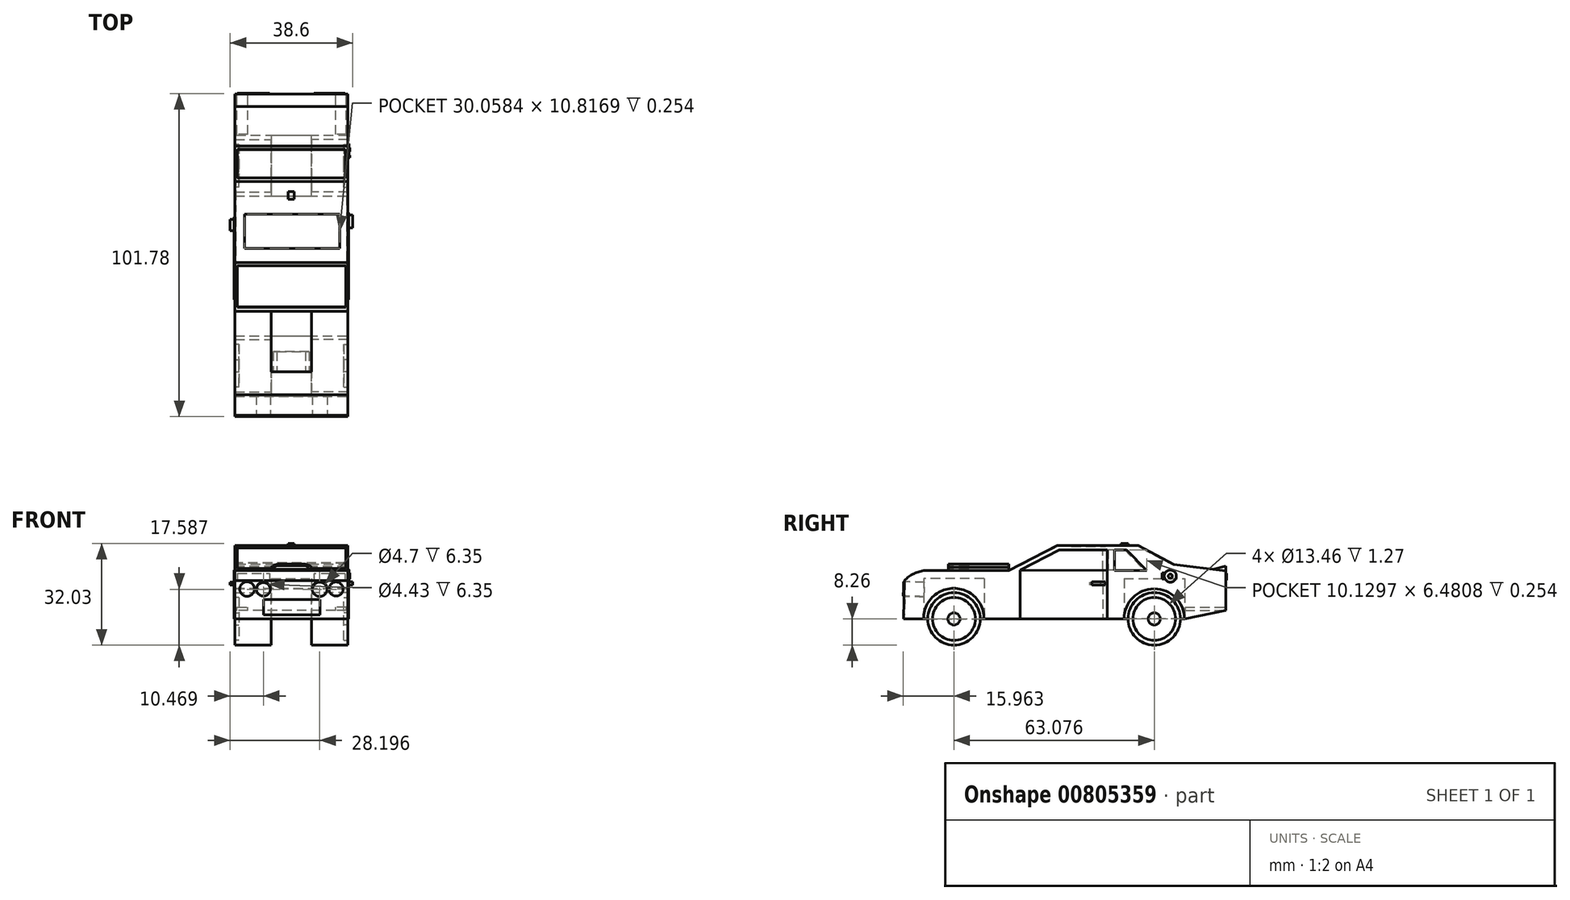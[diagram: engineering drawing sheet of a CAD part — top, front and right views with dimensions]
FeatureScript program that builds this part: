
annotation { "Feature Type Name" : "Feature", "Feature Type Description" : "" }
export const myFeature = defineFeature(function(context is Context, id is Id, definition is map)
    precondition{}
    {
        {
            var Q0;
            Q0=qCreatedBy(makeId("Right.planeOp"),FACE);
            var sketch = newSketch(context, id + "F0", { "sketchPlane" : qUnion([Q0])});
            skLineSegment(sketch, "E0", {"start": v(-101.04, 15.24) * mm, "end": v(-62.7, 15.24) * mm});
            skLineSegment(sketch, "E1", {"start": v(-62.7, 15.24) * mm, "end": v(-53, 23.14) * mm});
            skLineSegment(sketch, "E2", {"start": v(-53, 23.14) * mm, "end": v(-27.51, 23.14) * mm});
            skLineSegment(sketch, "E3", {"start": v(-27.51, 23.14) * mm, "end": v(-16.35, 17.16) * mm});
            skLineSegment(sketch, "E4", {"start": v(-16.35, 17.16) * mm, "end": v(0, 15.13) * mm});
            skLineSegment(sketch, "E5", {"start": v(0, 15.13) * mm, "end": v(0, 2.73) * mm});
            skLineSegment(sketch, "E6", {"start": v(0, 2.73) * mm, "end": v(-12.97, 0) * mm});
            skLineSegment(sketch, "E7", {"start": v(-12.97, 0) * mm, "end": v(-31.69, 0) * mm});
            skLineSegment(sketch, "E8", {"start": v(-31.69, 0) * mm, "end": v(-76.23, 0) * mm});
            skLineSegment(sketch, "E9", {"start": v(-76.23, 0) * mm, "end": v(-95.4, 0) * mm});
            skLineSegment(sketch, "E10", {"start": v(-95.4, 0) * mm, "end": v(-101.49, 0) * mm});
            skLineSegment(sketch, "E11", {"start": v(-101.49, 0) * mm, "end": v(-101.04, 15.24) * mm});
            skLineSegment(sketch, "E12", {"start": v(-53, 23.14) * mm, "end": v(-68.34, 15.24) * mm});
            skLineSegment(sketch, "E13", {"start": v(-68.34, 15.24) * mm, "end": v(-62.7, 15.24) * mm});
            skSolve(sketch);
        }
        {
            var Q0;
            Q0 = qSketchRegion(id + "F0", true);
            extrude(context, id + "F1", {"entities" : qUnion([Q0]), "depth" : 35.56 * mm, "offsetDistance" : 25.4 * mm});
        }
        {
            var Q0;
            Q0=makeQuery(id+"F1.opExtrude","CAP_FACE",FACE,{"disambiguationData":[OSD([sQuery(id+"F0.wireOp",EDGE,"E0"),sQuery(id+"F0.wireOp",EDGE,"E1"),sQuery(id+"F0.wireOp",EDGE,"E2"),sQuery(id+"F0.wireOp",EDGE,"E3"),sQuery(id+"F0.wireOp",EDGE,"E4"),sQuery(id+"F0.wireOp",EDGE,"E5"),sQuery(id+"F0.wireOp",EDGE,"E6"),sQuery(id+"F0.wireOp",EDGE,"E7"),sQuery(id+"F0.wireOp",EDGE,"E8"),sQuery(id+"F0.wireOp",EDGE,"E9"),sQuery(id+"F0.wireOp",EDGE,"E10"),sQuery(id+"F0.wireOp",EDGE,"E11")])],"isStart":false});
            var sketch = newSketch(context, id + "F2", { "sketchPlane" : qUnion([Q0])});
            skArc(sketch, "E14", {"start": v(-92.5, 15.24) * mm, "mid": v(-97.18, 14.66) * mm, "end": v(-101.13, 12.11) * mm});
            skSolve(sketch);
        }
        {
            var Q0;
            {var subQ0=sQuery(id+"F2.wireOp",EDGE,"E14");var subQ1=makeQuery(id+"F1.opExtrude","CAP_EDGE",EDGE,{"disambiguationData":[OSD([sQuery(id+"F0.wireOp",EDGE,"E11")])],"isStart":false});var subQ2=makeQuery(id+"F2.imprint","INTERSECT",VERTEX,{"derivedFrom":[subQ1,subQ0]});Q0=makeQuery(id+"F2.imprint","IMPRINT",FACE,{"disambiguationData":[TD([[makeQuery(id+"F2.imprint","IMPRINT",EDGE,{"disambiguationData":[TD([[subQ2,1.0]])],"derivedFrom":subQ0}),-1.0]])]});}
            extrude(context, id + "F3", {"entities" : qUnion([Q0]), "operationType" : NewBodyOperationType.REMOVE, "endBound" : BoundingType.THROUGH_ALL, "oppositeDirection" : true, "depth" : 25.4 * mm, "offsetDistance" : 25.4 * mm});
        }
        {
            var Q0;
            Q0=makeQuery(id+"F1.opExtrude","CAP_FACE",FACE,{"disambiguationData":[OSD([sQuery(id+"F0.wireOp",EDGE,"E0"),sQuery(id+"F0.wireOp",EDGE,"E1"),sQuery(id+"F0.wireOp",EDGE,"E2"),sQuery(id+"F0.wireOp",EDGE,"E3"),sQuery(id+"F0.wireOp",EDGE,"E4"),sQuery(id+"F0.wireOp",EDGE,"E5"),sQuery(id+"F0.wireOp",EDGE,"E6"),sQuery(id+"F0.wireOp",EDGE,"E7"),sQuery(id+"F0.wireOp",EDGE,"E8"),sQuery(id+"F0.wireOp",EDGE,"E9"),sQuery(id+"F0.wireOp",EDGE,"E10"),sQuery(id+"F0.wireOp",EDGE,"E11")])],"isStart":false});
            var sketch = newSketch(context, id + "F4", { "sketchPlane" : qUnion([Q0])});
            skLineSegment(sketch, "E15", {"start": v(-12.97, 0) * mm, "end": v(-32.02, 0) * mm, "construction": true});
            skLineSegment(sketch, "E16", {"start": v(-32.02, 0) * mm, "end": v(-22.5, 0) * mm, "construction": true});
            skLineSegment(sketch, "E17", {"start": v(-22.5, 0) * mm, "end": v(-22.5, 9.53) * mm, "construction": true});
            skLineSegment(sketch, "E18", {"start": v(-22.5, 9.53) * mm, "end": v(-22.5, -9.53) * mm, "construction": true});
            skLineSegment(sketch, "E19", {"start": v(-22.5, -9.53) * mm, "end": v(-22.5, 0) * mm, "construction": true});
            skLineSegment(sketch, "E20", {"start": v(-101.49, 0) * mm, "end": v(-95.14, 0) * mm, "construction": true});
            skLineSegment(sketch, "E21", {"start": v(-95.14, 0) * mm, "end": v(-76.09, 0) * mm, "construction": true});
            skLineSegment(sketch, "E22", {"start": v(-76.09, 0) * mm, "end": v(-85.61, 0) * mm, "construction": true});
            skLineSegment(sketch, "E23", {"start": v(-85.61, 0) * mm, "end": v(-85.61, 9.53) * mm, "construction": true});
            skLineSegment(sketch, "E24", {"start": v(-85.61, 9.53) * mm, "end": v(-85.61, -9.53) * mm, "construction": true});
            skArc(sketch, "E25", {"start": v(-76.09, 0) * mm, "mid": v(-85.61, 9.68) * mm, "end": v(-95.14, 0) * mm});
            skArc(sketch, "E26", {"start": v(-12.97, 0) * mm, "mid": v(-22.5, 9.51) * mm, "end": v(-32.02, 0) * mm});
            skLineSegment(sketch, "E27", {"start": v(-95.14, 0) * mm, "end": v(-76.09, 0) * mm});
            skLineSegment(sketch, "E28", {"start": v(-32.02, 0) * mm, "end": v(-12.97, 0) * mm});
            skArc(sketch, "E29", {"start": v(-76.09, 0) * mm, "mid": v(-85.61, 9.64) * mm, "end": v(-95.14, 0) * mm});
            skArc(sketch, "E30", {"start": v(-12.97, 0) * mm, "mid": v(-22.5, 9.49) * mm, "end": v(-32.02, 0) * mm});
            skSolve(sketch);
        }
        {
            var Q0;
            Q0=makeQuery(id+"F4.imprint","IMPRINT",FACE,{"disambiguationData":[TD([[makeQuery(id+"F4.imprint","IMPRINT",EDGE,{"derivedFrom":sQuery(id+"F4.wireOp",EDGE,"E27")}),-1.0]])]});
            var Q1;
            Q1=makeQuery(id+"F4.imprint","IMPRINT",FACE,{"disambiguationData":[TD([[makeQuery(id+"F4.imprint","IMPRINT",EDGE,{"derivedFrom":sQuery(id+"F4.wireOp",EDGE,"E28")}),-1.0]])]});
            extrude(context, id + "F5", {"entities" : qUnion([Q0, Q1]), "operationType" : NewBodyOperationType.REMOVE, "endBound" : BoundingType.THROUGH_ALL, "oppositeDirection" : true, "depth" : 25.4 * mm, "offsetDistance" : 25.4 * mm});
        }
        {
            var Q0;
            Q0=makeQuery(id+"F1.opExtrude","CAP_FACE",FACE,{"disambiguationData":[OSD([sQuery(id+"F0.wireOp",EDGE,"E0"),sQuery(id+"F0.wireOp",EDGE,"E1"),sQuery(id+"F0.wireOp",EDGE,"E2"),sQuery(id+"F0.wireOp",EDGE,"E3"),sQuery(id+"F0.wireOp",EDGE,"E4"),sQuery(id+"F0.wireOp",EDGE,"E5"),sQuery(id+"F0.wireOp",EDGE,"E6"),sQuery(id+"F0.wireOp",EDGE,"E7"),sQuery(id+"F0.wireOp",EDGE,"E8"),sQuery(id+"F0.wireOp",EDGE,"E9"),sQuery(id+"F0.wireOp",EDGE,"E10"),sQuery(id+"F0.wireOp",EDGE,"E11")])],"isStart":false});
            var sketch = newSketch(context, id + "F6", { "sketchPlane" : qUnion([Q0])});
            skLineSegment(sketch, "E31", {"start": v(0, 15.13) * mm, "end": v(0, 16.66) * mm});
            skLineSegment(sketch, "E32", {"start": v(0, 16.66) * mm, "end": v(-3.84, 15.6) * mm});
            skSolve(sketch);
        }
        {
            var Q0;
            {var subQ0=sQuery(id+"F6.wireOp",EDGE,"E31");Q0=makeQuery(id+"F6.imprint","IMPRINT",FACE,{"disambiguationData":[TD([[makeQuery(id+"F6.imprint","IMPRINT",EDGE,{"derivedFrom":subQ0}),1.0]])]});}
            extrude(context, id + "F7", {"entities" : qUnion([Q0]), "oppositeDirection" : true, "depth" : 35.56 * mm, "offsetDistance" : 25.4 * mm});
        }
        {
            var Q0;
            Q0=makeQuery(id+"F1.opExtrude","SWEPT_FACE",FACE,{"disambiguationData":[OSD([sQuery(id+"F0.wireOp",EDGE,"E2")])]});
            var sketch = newSketch(context, id + "F8", { "sketchPlane" : qUnion([Q0])});
            skLineSegment(sketch, "E33", {"start": v(17.78, -33.03) * mm, "end": v(18.6, -33.03) * mm});
            skPoint(sketch, "E33.startSnap0", {"position": v(17.78, -27.51) * mm});
            skLineSegment(sketch, "E34", {"start": v(18.6, -33.03) * mm, "end": v(18.6, -30.66) * mm});
            skLineSegment(sketch, "E35", {"start": v(18.6, -30.66) * mm, "end": v(16.76, -30.66) * mm});
            skLineSegment(sketch, "E36", {"start": v(16.76, -30.66) * mm, "end": v(16.76, -33.03) * mm});
            skLineSegment(sketch, "E37", {"start": v(16.76, -33.03) * mm, "end": v(17.78, -33.03) * mm});
            skSolve(sketch);
        }
        {
            var Q0;
            Q0 = qSketchRegion(id + "F8", true);
            extrude(context, id + "F9", {"entities" : qUnion([Q0]), "operationType" : NewBodyOperationType.ADD, "depth" : 0.64 * mm, "offsetDistance" : 25.4 * mm});
        }
        {
            var Q0;
            Q0=makeQuery(id+"F1.opExtrude","SWEPT_FACE",FACE,{"disambiguationData":[OSD([sQuery(id+"F0.wireOp",EDGE,"E2")])]});
            var sketch = newSketch(context, id + "F10", { "sketchPlane" : qUnion([Q0])});
            skLineSegment(sketch, "E38.bottom", {"start": v(2.98, -48.61) * mm, "end": v(33.04, -48.61) * mm});
            skLineSegment(sketch, "E38.top", {"start": v(2.98, -37.8) * mm, "end": v(33.04, -37.8) * mm});
            skLineSegment(sketch, "E38.left", {"start": v(2.98, -48.61) * mm, "end": v(2.98, -37.8) * mm});
            skLineSegment(sketch, "E38.right", {"start": v(33.04, -48.61) * mm, "end": v(33.04, -37.8) * mm});
            skSolve(sketch);
        }
        {
            var Q0;
            Q0 = qSketchRegion(id + "F10", true);
            extrude(context, id + "F11", {"entities" : qUnion([Q0]), "operationType" : NewBodyOperationType.REMOVE, "oppositeDirection" : true, "depth" : 0.25 * mm, "offsetDistance" : 25.4 * mm});
        }
        {
            var Q0;
            {var subQ2=sQuery(id+"F0.wireOp",EDGE,"E10");var subQ3=sQuery(id+"F0.wireOp",EDGE,"E9");var subQ4=sQuery(id+"F0.wireOp",EDGE,"E8");var subQ5=sQuery(id+"F0.wireOp",EDGE,"E7");Q0=makeQuery(id+"F5.boolean.opBoolean","SPLIT",FACE,{"disambiguationData":[TD([makeQuery(id+"F5.opExtrude","SWEPT_FACE",FACE,{"disambiguationData":[OSD([sQuery(id+"F4.wireOp",EDGE,"E30")])]})])],"derivedFrom":makeQuery(id+"F1.opExtrude","SWEPT_FACE",FACE,{"disambiguationData":[OSD([subQ5,subQ4,subQ3,subQ2])]})});}
            var sketch = newSketch(context, id + "F12", { "sketchPlane" : qUnion([Q0])});
            skLineSegment(sketch, "E39", {"start": v(17.78, 76.09) * mm, "end": v(24.13, 76.09) * mm});
            skLineSegment(sketch, "E40", {"start": v(24.13, 76.09) * mm, "end": v(11.43, 76.09) * mm});
            skLineSegment(sketch, "E41", {"start": v(11.43, 76.09) * mm, "end": v(11.43, 95.04) * mm});
            skLineSegment(sketch, "E42", {"start": v(11.43, 95.04) * mm, "end": v(24.13, 95.04) * mm});
            skLineSegment(sketch, "E43", {"start": v(24.13, 95.04) * mm, "end": v(24.13, 76.09) * mm});
            skSolve(sketch);
        }
        {
            var Q0;
            Q0 = qSketchRegion(id + "F12", true);
            extrude(context, id + "F13", {"entities" : qUnion([Q0]), "oppositeDirection" : true, "depth" : 12.7 * mm, "offsetDistance" : 25.4 * mm});
        }
        {
            var Q0;
            {var subQ2=sQuery(id+"F0.wireOp",EDGE,"E10");var subQ3=sQuery(id+"F0.wireOp",EDGE,"E9");var subQ4=sQuery(id+"F0.wireOp",EDGE,"E8");var subQ5=sQuery(id+"F0.wireOp",EDGE,"E7");Q0=makeQuery(id+"F5.boolean.opBoolean","SPLIT",FACE,{"disambiguationData":[TD([makeQuery(id+"F5.opExtrude","SWEPT_FACE",FACE,{"disambiguationData":[OSD([sQuery(id+"F4.wireOp",EDGE,"E30")])]})])],"derivedFrom":makeQuery(id+"F1.opExtrude","SWEPT_FACE",FACE,{"disambiguationData":[OSD([subQ5,subQ4,subQ3,subQ2])]})});}
            var sketch = newSketch(context, id + "F14", { "sketchPlane" : qUnion([Q0])});
            skLineSegment(sketch, "E44", {"start": v(17.78, 32.02) * mm, "end": v(11.43, 32.02) * mm});
            skLineSegment(sketch, "E45", {"start": v(11.43, 32.02) * mm, "end": v(24.13, 32.02) * mm});
            skLineSegment(sketch, "E46", {"start": v(24.13, 32.02) * mm, "end": v(24.13, 12.97) * mm});
            skLineSegment(sketch, "E47", {"start": v(24.13, 12.97) * mm, "end": v(11.43, 12.97) * mm});
            skLineSegment(sketch, "E48", {"start": v(11.43, 12.97) * mm, "end": v(11.43, 32.02) * mm});
            skSolve(sketch);
        }
        {
            var Q0;
            Q0 = qSketchRegion(id + "F14", true);
            extrude(context, id + "F15", {"entities" : qUnion([Q0]), "oppositeDirection" : true, "depth" : 12.7 * mm, "offsetDistance" : 25.4 * mm});
        }
        {
            var Q0;
            Q0=makeQuery(id+"F1.opExtrude","SWEPT_FACE",FACE,{"disambiguationData":[OSD([sQuery(id+"F0.wireOp",EDGE,"E12")])]});
            var sketch = newSketch(context, id + "F16", { "sketchPlane" : qUnion([Q0])});
            skLineSegment(sketch, "E49.bottom", {"start": v(0.7, -37.65) * mm, "end": v(34.9, -37.65) * mm});
            skLineSegment(sketch, "E49.top", {"start": v(0.7, -52.42) * mm, "end": v(34.9, -52.42) * mm});
            skLineSegment(sketch, "E49.left", {"start": v(0.7, -37.65) * mm, "end": v(0.7, -52.42) * mm});
            skLineSegment(sketch, "E49.right", {"start": v(34.9, -37.65) * mm, "end": v(34.9, -52.42) * mm});
            skSolve(sketch);
        }
        {
            var Q0;
            Q0 = qSketchRegion(id + "F16", true);
            extrude(context, id + "F17", {"entities" : qUnion([Q0]), "operationType" : NewBodyOperationType.REMOVE, "oppositeDirection" : true, "depth" : 0.25 * mm, "offsetDistance" : 25.4 * mm});
        }
        {
            var Q0;
            Q0=makeQuery(id+"F1.opExtrude","SWEPT_FACE",FACE,{"disambiguationData":[OSD([sQuery(id+"F0.wireOp",EDGE,"E0")])]});
            var sketch = newSketch(context, id + "F18", { "sketchPlane" : qUnion([Q0])});
            skLineSegment(sketch, "E50", {"start": v(17.78, -68.34) * mm, "end": v(24.13, -68.34) * mm});
            skLineSegment(sketch, "E51", {"start": v(24.13, -68.34) * mm, "end": v(11.43, -68.34) * mm});
            skLineSegment(sketch, "E52", {"start": v(11.43, -68.34) * mm, "end": v(11.43, -87.39) * mm});
            skLineSegment(sketch, "E53", {"start": v(11.43, -87.39) * mm, "end": v(24.13, -87.39) * mm});
            skLineSegment(sketch, "E54", {"start": v(24.13, -87.39) * mm, "end": v(24.13, -68.34) * mm});
            skSolve(sketch);
        }
        {
            var Q0;
            Q0 = qSketchRegion(id + "F18", true);
            extrude(context, id + "F19", {"entities" : qUnion([Q0]), "operationType" : NewBodyOperationType.ADD, "depth" : 2.03 * mm, "offsetDistance" : 25.4 * mm});
        }
        {
            var Q0;
            Q0=makeQuery(id+"F19.opExtrude","SWEPT_FACE",FACE,{"disambiguationData":[OSD([sQuery(id+"F18.wireOp",EDGE,"E53")])]});
            var sketch = newSketch(context, id + "F20", { "sketchPlane" : qUnion([Q0])});
            skLineSegment(sketch, "E55", {"start": v(11.43, 17.28) * mm, "end": v(13.97, 17.28) * mm, "construction": true});
            skLineSegment(sketch, "E56", {"start": v(24.13, 17.28) * mm, "end": v(21.6, 17.28) * mm, "construction": true});
            skArc(sketch, "E57", {"start": v(13.97, 17.28) * mm, "mid": v(12.6, 17.01) * mm, "end": v(11.43, 16.26) * mm});
            skArc(sketch, "E58", {"start": v(24.13, 16.26) * mm, "mid": v(22.96, 17.01) * mm, "end": v(21.6, 17.28) * mm});
            skLineSegment(sketch, "E59", {"start": v(11.43, 16.26) * mm, "end": v(11.43, 17.28) * mm});
            skLineSegment(sketch, "E60", {"start": v(24.13, 16.26) * mm, "end": v(24.13, 17.28) * mm});
            skSolve(sketch);
        }
        {
            var Q0;
            {var subQ0=sQuery(id+"F20.wireOp",EDGE,"E57");Q0=makeQuery(id+"F20.imprint","IMPRINT",FACE,{"disambiguationData":[TD([[makeQuery(id+"F20.imprint","IMPRINT",EDGE,{"derivedFrom":subQ0}),-1.0]])]});}
            var Q1;
            {var subQ0=sQuery(id+"F20.wireOp",EDGE,"E58");Q1=makeQuery(id+"F20.imprint","IMPRINT",FACE,{"disambiguationData":[TD([[makeQuery(id+"F20.imprint","IMPRINT",EDGE,{"derivedFrom":subQ0}),-1.0]])]});}
            extrude(context, id + "F21", {"entities" : qUnion([Q0, Q1]), "operationType" : NewBodyOperationType.REMOVE, "oppositeDirection" : true, "depth" : 19.05 * mm, "offsetDistance" : 25.4 * mm});
        }
        {
            var Q0;
            Q0=makeQuery(id+"F19.opExtrude","SWEPT_FACE",FACE,{"disambiguationData":[OSD([sQuery(id+"F18.wireOp",EDGE,"E53")])]});
            var sketch = newSketch(context, id + "F22", { "sketchPlane" : qUnion([Q0])});
            skLineSegment(sketch, "E61", {"start": v(12.1, 15.64) * mm, "end": v(12.1, 16.14) * mm});
            skLineSegment(sketch, "E62", {"start": v(12.1, 16.14) * mm, "end": v(13.23, 16.71) * mm});
            skLineSegment(sketch, "E63", {"start": v(13.23, 16.71) * mm, "end": v(22.2, 16.71) * mm});
            skLineSegment(sketch, "E64", {"start": v(22.2, 16.71) * mm, "end": v(23.34, 16.14) * mm});
            skLineSegment(sketch, "E65", {"start": v(23.34, 16.14) * mm, "end": v(23.34, 15.64) * mm});
            skLineSegment(sketch, "E66", {"start": v(23.34, 15.64) * mm, "end": v(12.1, 15.64) * mm});
            skSolve(sketch);
        }
        {
            var Q0;
            Q0 = qSketchRegion(id + "F22", true);
            extrude(context, id + "F23", {"entities" : qUnion([Q0]), "operationType" : NewBodyOperationType.REMOVE, "oppositeDirection" : true, "depth" : 6.35 * mm, "offsetDistance" : 25.4 * mm});
        }
        {
            var Q0;
            Q0=makeQuery(id+"F1.opExtrude","CAP_FACE",FACE,{"disambiguationData":[OSD([sQuery(id+"F0.wireOp",EDGE,"E0"),sQuery(id+"F0.wireOp",EDGE,"E2"),sQuery(id+"F0.wireOp",EDGE,"E3"),sQuery(id+"F0.wireOp",EDGE,"E4"),sQuery(id+"F0.wireOp",EDGE,"E5"),sQuery(id+"F0.wireOp",EDGE,"E6"),sQuery(id+"F0.wireOp",EDGE,"E7"),sQuery(id+"F0.wireOp",EDGE,"E8"),sQuery(id+"F0.wireOp",EDGE,"E9"),sQuery(id+"F0.wireOp",EDGE,"E10"),sQuery(id+"F0.wireOp",EDGE,"E11"),sQuery(id+"F0.wireOp",EDGE,"E12")])],"isStart":false});
            var sketch = newSketch(context, id + "F24", { "sketchPlane" : qUnion([Q0])});
            skCircle(sketch, "E67", {"center": v(-17.43, 13.49) * mm, "radius": 1.9 * mm});
            skSolve(sketch);
        }
        {
            var Q0;
            Q0 = qSketchRegion(id + "F24", true);
            extrude(context, id + "F25", {"entities" : qUnion([Q0]), "operationType" : NewBodyOperationType.ADD, "depth" : 0.38 * mm, "offsetDistance" : 25.4 * mm});
        }
        {
            var Q0;
            Q0=makeQuery(id+"F25.opExtrude","CAP_FACE",FACE,{"disambiguationData":[OSD([sQuery(id+"F24.wireOp",EDGE,"E67")])],"isStart":false});
            var sketch = newSketch(context, id + "F26", { "sketchPlane" : qUnion([Q0])});
            skCircle(sketch, "E68", {"center": v(-17.43, 13.49) * mm, "radius": 0.64 * mm});
            skSolve(sketch);
        }
        {
            var Q0;
            Q0 = qSketchRegion(id + "F26", true);
            extrude(context, id + "F27", {"entities" : qUnion([Q0]), "operationType" : NewBodyOperationType.ADD, "depth" : 0.25 * mm, "offsetDistance" : 25.4 * mm});
        }
        {
            var Q0;
            Q0=makeQuery(id+"F13.opExtrude","SWEPT_FACE",FACE,{"disambiguationData":[OSD([sQuery(id+"F12.wireOp",EDGE,"E43")])]});
            var sketch = newSketch(context, id + "F28", { "sketchPlane" : qUnion([Q0])});
            skCircle(sketch, "E69", {"center": v(-85.57, 0) * mm, "radius": 8.26 * mm});
            skSolve(sketch);
        }
        {
            var Q0;
            Q0 = qSketchRegion(id + "F28", true);
            extrude(context, id + "F29", {"entities" : qUnion([Q0]), "operationType" : NewBodyOperationType.ADD, "depth" : 11.43 * mm, "offsetDistance" : 25.4 * mm});
        }
        {
            var Q0;
            Q0=makeQuery(id+"F29.opExtrude","CAP_FACE",FACE,{"disambiguationData":[OSD([sQuery(id+"F28.wireOp",EDGE,"E69")])],"isStart":false});
            var sketch = newSketch(context, id + "F30", { "sketchPlane" : qUnion([Q0])});
            skCircle(sketch, "E70", {"center": v(-85.57, 0) * mm, "radius": 6.73 * mm});
            skSolve(sketch);
        }
        {
            var Q0;
            Q0 = qSketchRegion(id + "F30", true);
            extrude(context, id + "F31", {"entities" : qUnion([Q0]), "operationType" : NewBodyOperationType.REMOVE, "oppositeDirection" : true, "depth" : 1.27 * mm, "offsetDistance" : 25.4 * mm});
        }
        {
            var Q0;
            Q0=makeQuery(id+"F31.boolean.opBoolean","COPY",FACE,{"derivedFrom":makeQuery(id+"F31.opExtrude","CAP_FACE",FACE,{"disambiguationData":[OSD([sQuery(id+"F30.wireOp",EDGE,"E70")])],"isStart":false})});
            var sketch = newSketch(context, id + "F32", { "sketchPlane" : qUnion([Q0])});
            skCircle(sketch, "E71", {"center": v(-85.57, 0) * mm, "radius": 1.9 * mm});
            skSolve(sketch);
        }
        {
            var Q0;
            Q0 = qSketchRegion(id + "F32", true);
            extrude(context, id + "F33", {"entities" : qUnion([Q0]), "operationType" : NewBodyOperationType.ADD, "depth" : 1.27 * mm, "offsetDistance" : 25.4 * mm});
        }
        {
            var Q0;
            Q0=makeQuery(id+"F15.opExtrude","SWEPT_FACE",FACE,{"disambiguationData":[OSD([sQuery(id+"F14.wireOp",EDGE,"E46")])]});
            var sketch = newSketch(context, id + "F34", { "sketchPlane" : qUnion([Q0])});
            skCircle(sketch, "E72", {"center": v(-22.5, 0) * mm, "radius": 8.26 * mm});
            skSolve(sketch);
        }
        {
            var Q0;
            Q0 = qSketchRegion(id + "F34", true);
            extrude(context, id + "F35", {"entities" : qUnion([Q0]), "operationType" : NewBodyOperationType.ADD, "depth" : 11.43 * mm, "offsetDistance" : 25.4 * mm});
        }
        {
            var Q0;
            Q0=makeQuery(id+"F35.opExtrude","CAP_FACE",FACE,{"disambiguationData":[OSD([sQuery(id+"F34.wireOp",EDGE,"E72")])],"isStart":false});
            var sketch = newSketch(context, id + "F36", { "sketchPlane" : qUnion([Q0])});
            skCircle(sketch, "E73", {"center": v(-22.5, 0) * mm, "radius": 6.73 * mm});
            skSolve(sketch);
        }
        {
            var Q0;
            Q0 = qSketchRegion(id + "F36", true);
            extrude(context, id + "F37", {"entities" : qUnion([Q0]), "operationType" : NewBodyOperationType.REMOVE, "oppositeDirection" : true, "depth" : 1.27 * mm, "offsetDistance" : 25.4 * mm});
        }
        {
            var Q0;
            Q0=makeQuery(id+"F37.boolean.opBoolean","COPY",FACE,{"derivedFrom":makeQuery(id+"F37.opExtrude","CAP_FACE",FACE,{"disambiguationData":[OSD([sQuery(id+"F36.wireOp",EDGE,"E73")])],"isStart":false})});
            var sketch = newSketch(context, id + "F38", { "sketchPlane" : qUnion([Q0])});
            skCircle(sketch, "E74", {"center": v(-22.5, 0) * mm, "radius": 1.9 * mm});
            skSolve(sketch);
        }
        {
            var Q0;
            Q0 = qSketchRegion(id + "F38", true);
            extrude(context, id + "F39", {"entities" : qUnion([Q0]), "operationType" : NewBodyOperationType.ADD, "depth" : 1.27 * mm, "offsetDistance" : 25.4 * mm});
        }
        {
            var Q0;
            Q0=makeQuery(id+"F1.opExtrude","CAP_FACE",FACE,{"disambiguationData":[OSD([sQuery(id+"F0.wireOp",EDGE,"E0"),sQuery(id+"F0.wireOp",EDGE,"E2"),sQuery(id+"F0.wireOp",EDGE,"E3"),sQuery(id+"F0.wireOp",EDGE,"E4"),sQuery(id+"F0.wireOp",EDGE,"E5"),sQuery(id+"F0.wireOp",EDGE,"E6"),sQuery(id+"F0.wireOp",EDGE,"E7"),sQuery(id+"F0.wireOp",EDGE,"E8"),sQuery(id+"F0.wireOp",EDGE,"E9"),sQuery(id+"F0.wireOp",EDGE,"E10"),sQuery(id+"F0.wireOp",EDGE,"E11"),sQuery(id+"F0.wireOp",EDGE,"E12")])],"isStart":false});
            var sketch = newSketch(context, id + "F40", { "sketchPlane" : qUnion([Q0])});
            skArc(sketch, "E75", {"start": v(-19.19, 14.43) * mm, "mid": v(-19.4, 13.53) * mm, "end": v(-19.22, 12.61) * mm});
            skLineSegment(sketch, "E76", {"start": v(-19.22, 12.61) * mm, "end": v(-20.04, 12.61) * mm});
            skLineSegment(sketch, "E77", {"start": v(-20.04, 12.61) * mm, "end": v(-20.04, 14.42) * mm});
            skLineSegment(sketch, "E78", {"start": v(-20.04, 14.42) * mm, "end": v(-19.19, 14.43) * mm});
            skSolve(sketch);
        }
        {
            var Q0;
            Q0 = qSketchRegion(id + "F40", true);
            extrude(context, id + "F41", {"entities" : qUnion([Q0]), "operationType" : NewBodyOperationType.ADD, "depth" : 0.64 * mm, "offsetDistance" : 25.4 * mm});
        }
        {
            var Q0;
            Q0=makeQuery(id+"F15.opExtrude","SWEPT_FACE",FACE,{"disambiguationData":[OSD([sQuery(id+"F14.wireOp",EDGE,"E48")])]});
            var sketch = newSketch(context, id + "F42", { "sketchPlane" : qUnion([Q0])});
            skCircle(sketch, "E79", {"center": v(22.5, 0) * mm, "radius": 8.26 * mm});
            skSolve(sketch);
        }
        {
            var Q0;
            Q0 = qSketchRegion(id + "F42", true);
            extrude(context, id + "F43", {"entities" : qUnion([Q0]), "operationType" : NewBodyOperationType.ADD, "depth" : 11.43 * mm, "offsetDistance" : 25.4 * mm});
        }
        {
            var Q0;
            Q0=makeQuery(id+"F43.opExtrude","CAP_FACE",FACE,{"disambiguationData":[OSD([sQuery(id+"F42.wireOp",EDGE,"E79")])],"isStart":false});
            var sketch = newSketch(context, id + "F44", { "sketchPlane" : qUnion([Q0])});
            skCircle(sketch, "E80", {"center": v(22.5, 0) * mm, "radius": 6.73 * mm});
            skSolve(sketch);
        }
        {
            var Q0;
            Q0 = qSketchRegion(id + "F44", true);
            extrude(context, id + "F45", {"entities" : qUnion([Q0]), "operationType" : NewBodyOperationType.REMOVE, "oppositeDirection" : true, "depth" : 1.27 * mm, "offsetDistance" : 25.4 * mm});
        }
        {
            var Q0;
            Q0=makeQuery(id+"F45.boolean.opBoolean","COPY",FACE,{"derivedFrom":makeQuery(id+"F45.opExtrude","CAP_FACE",FACE,{"disambiguationData":[OSD([sQuery(id+"F44.wireOp",EDGE,"E80")])],"isStart":false})});
            var sketch = newSketch(context, id + "F46", { "sketchPlane" : qUnion([Q0])});
            skCircle(sketch, "E81", {"center": v(22.5, 0) * mm, "radius": 1.9 * mm});
            skSolve(sketch);
        }
        {
            var Q0;
            Q0 = qSketchRegion(id + "F46", true);
            extrude(context, id + "F47", {"entities" : qUnion([Q0]), "operationType" : NewBodyOperationType.ADD, "depth" : 1.27 * mm, "offsetDistance" : 25.4 * mm});
        }
        {
            var Q0;
            Q0=makeQuery(id+"F13.opExtrude","SWEPT_FACE",FACE,{"disambiguationData":[OSD([sQuery(id+"F12.wireOp",EDGE,"E41")])]});
            var sketch = newSketch(context, id + "F48", { "sketchPlane" : qUnion([Q0])});
            skCircle(sketch, "E82", {"center": v(85.57, 0) * mm, "radius": 8.26 * mm});
            skSolve(sketch);
        }
        {
            var Q0;
            {var subQ0=sQuery(id+"F48.wireOp",EDGE,"E82");var subQ1=makeQuery(id+"F13.opExtrude","CAP_EDGE",EDGE,{"disambiguationData":[OSD([sQuery(id+"F12.wireOp",EDGE,"E41")])],"isStart":true});var subQ2=makeQuery(id+"F48.imprint","INTERSECT",VERTEX,{"disambiguationData":[OD(0.0)],"derivedFrom":[subQ1,subQ0]});Q0=makeQuery(id+"F48.imprint","IMPRINT",FACE,{"disambiguationData":[TD([[makeQuery(id+"F48.imprint","IMPRINT",EDGE,{"disambiguationData":[TD([[subQ2,-1.0]])],"derivedFrom":subQ0}),1.0]])]});}
            var Q1;
            {var subQ0=sQuery(id+"F48.wireOp",EDGE,"E82");var subQ1=makeQuery(id+"F13.opExtrude","CAP_EDGE",EDGE,{"disambiguationData":[OSD([sQuery(id+"F12.wireOp",EDGE,"E41")])],"isStart":true});var subQ2=makeQuery(id+"F48.imprint","INTERSECT",VERTEX,{"disambiguationData":[OD(0.0)],"derivedFrom":[subQ1,subQ0]});Q1=makeQuery(id+"F48.imprint","IMPRINT",FACE,{"disambiguationData":[TD([[makeQuery(id+"F48.imprint","IMPRINT",EDGE,{"disambiguationData":[TD([[subQ2,1.0]])],"derivedFrom":subQ0}),1.0]])]});}
            extrude(context, id + "F49", {"entities" : qUnion([Q0, Q1]), "operationType" : NewBodyOperationType.ADD, "depth" : 11.43 * mm, "offsetDistance" : 25.4 * mm});
        }
        {
            var Q0;
            Q0=makeQuery(id+"F49.opExtrude","CAP_FACE",FACE,{"disambiguationData":[OSD([sQuery(id+"F48.wireOp",EDGE,"E82")])],"isStart":false});
            var sketch = newSketch(context, id + "F50", { "sketchPlane" : qUnion([Q0])});
            skCircle(sketch, "E83", {"center": v(85.57, 0) * mm, "radius": 6.73 * mm});
            skSolve(sketch);
        }
        {
            var Q0;
            Q0=makeQuery(id+"F50.imprint","IMPRINT",FACE,{"disambiguationData":[TD([[makeQuery(id+"F50.imprint","IMPRINT",EDGE,{"derivedFrom":sQuery(id+"F50.wireOp",EDGE,"E83")}),1.0]])]});
            extrude(context, id + "F51", {"entities" : qUnion([Q0]), "operationType" : NewBodyOperationType.REMOVE, "oppositeDirection" : true, "depth" : 1.27 * mm, "offsetDistance" : 25.4 * mm});
        }
        {
            var Q0;
            Q0=makeQuery(id+"F51.boolean.opBoolean","COPY",FACE,{"derivedFrom":makeQuery(id+"F51.opExtrude","CAP_FACE",FACE,{"disambiguationData":[OSD([sQuery(id+"F50.wireOp",EDGE,"E83")])],"isStart":false})});
            var sketch = newSketch(context, id + "F52", { "sketchPlane" : qUnion([Q0])});
            skCircle(sketch, "E84", {"center": v(85.57, 0) * mm, "radius": 1.9 * mm});
            skSolve(sketch);
        }
        {
            var Q0;
            Q0 = qSketchRegion(id + "F52", true);
            extrude(context, id + "F53", {"entities" : qUnion([Q0]), "operationType" : NewBodyOperationType.ADD, "depth" : 1.27 * mm, "offsetDistance" : 25.4 * mm});
        }
        {
            var Q0;
            Q0=makeQuery(id+"F1.opExtrude","CAP_FACE",FACE,{"disambiguationData":[OSD([sQuery(id+"F0.wireOp",EDGE,"E0"),sQuery(id+"F0.wireOp",EDGE,"E2"),sQuery(id+"F0.wireOp",EDGE,"E3"),sQuery(id+"F0.wireOp",EDGE,"E4"),sQuery(id+"F0.wireOp",EDGE,"E5"),sQuery(id+"F0.wireOp",EDGE,"E6"),sQuery(id+"F0.wireOp",EDGE,"E7"),sQuery(id+"F0.wireOp",EDGE,"E8"),sQuery(id+"F0.wireOp",EDGE,"E9"),sQuery(id+"F0.wireOp",EDGE,"E10"),sQuery(id+"F0.wireOp",EDGE,"E11"),sQuery(id+"F0.wireOp",EDGE,"E12")])],"isStart":false});
            var sketch = newSketch(context, id + "F54", { "sketchPlane" : qUnion([Q0])});
            skLineSegment(sketch, "E85", {"start": v(-64.77, 15.36) * mm, "end": v(-52.4, 21.73) * mm});
            skLineSegment(sketch, "E86", {"start": v(-52.4, 21.73) * mm, "end": v(-31.2, 21.73) * mm});
            skLineSegment(sketch, "E87", {"start": v(-31.2, 21.73) * mm, "end": v(-24.9, 15.24) * mm});
            skLineSegment(sketch, "E88", {"start": v(-24.9, 15.24) * mm, "end": v(-65.9, 15.36) * mm});
            skLineSegment(sketch, "E89", {"start": v(-34.58, 21.73) * mm, "end": v(-34.58, 15.27) * mm});
            skLineSegment(sketch, "E90", {"start": v(-34.58, 15.27) * mm, "end": v(-34.58, 0) * mm});
            skLineSegment(sketch, "E91", {"start": v(-34.58, 0) * mm, "end": v(-64.77, 0) * mm});
            skLineSegment(sketch, "E92", {"start": v(-64.77, 0) * mm, "end": v(-64.77, 15.36) * mm});
            skSolve(sketch);
        }
        {
            var Q0;
            {var subQ2=sQuery(id+"F54.wireOp",EDGE,"E85");Q0=makeQuery(id+"F54.imprint","IMPRINT",FACE,{"disambiguationData":[TD([[makeQuery(id+"F54.imprint","IMPRINT",EDGE,{"derivedFrom":subQ2}),-1.0]])]});}
            var Q1;
            {var subQ0=sQuery(id+"F54.wireOp",EDGE,"E87");Q1=makeQuery(id+"F54.imprint","IMPRINT",FACE,{"disambiguationData":[TD([[makeQuery(id+"F54.imprint","IMPRINT",EDGE,{"derivedFrom":subQ0}),-1.0]])]});}
            extrude(context, id + "F55", {"entities" : qUnion([Q0, Q1]), "operationType" : NewBodyOperationType.REMOVE, "oppositeDirection" : true, "depth" : 0.25 * mm, "offsetDistance" : 25.4 * mm});
        }
        {
            var Q0;
            Q0=makeQuery(id+"F55.boolean.opBoolean","COPY",FACE,{"derivedFrom":makeQuery(id+"F55.opExtrude","CAP_FACE",FACE,{"disambiguationData":[OSD([sQuery(id+"F54.wireOp",EDGE,"E85"),sQuery(id+"F54.wireOp",EDGE,"E86"),sQuery(id+"F54.wireOp",EDGE,"E87"),sQuery(id+"F54.wireOp",EDGE,"E88"),sQuery(id+"F54.wireOp",EDGE,"E92")])],"isStart":false})});
            var sketch = newSketch(context, id + "F56", { "sketchPlane" : qUnion([Q0])});
            skLineSegment(sketch, "E93", {"start": v(-35.02, 21.73) * mm, "end": v(-35.02, 15.27) * mm});
            skLineSegment(sketch, "E94", {"start": v(-35.02, 15.27) * mm, "end": v(-37.24, 15.28) * mm});
            skLineSegment(sketch, "E95", {"start": v(-37.24, 15.28) * mm, "end": v(-37.24, 21.73) * mm});
            skLineSegment(sketch, "E96", {"start": v(-37.24, 21.73) * mm, "end": v(-35.02, 21.73) * mm});
            skSolve(sketch);
        }
        {
            var Q0;
            Q0=makeQuery(id+"F56.imprint","IMPRINT",FACE,{"disambiguationData":[TD([[makeQuery(id+"F56.imprint","IMPRINT",EDGE,{"derivedFrom":sQuery(id+"F56.wireOp",EDGE,"E93")}),-1.0]])]});
            extrude(context, id + "F57", {"entities" : qUnion([Q0]), "operationType" : NewBodyOperationType.ADD, "depth" : 0.25 * mm, "offsetDistance" : 25.4 * mm});
        }
        {
            var Q0;
            Q0=makeQuery(id+"F57.boolean.opBoolean","MERGE",FACE,{"derivedFrom":[makeQuery(id+"F1.opExtrude","CAP_FACE",FACE,{"disambiguationData":[OSD([sQuery(id+"F0.wireOp",EDGE,"E0"),sQuery(id+"F0.wireOp",EDGE,"E2"),sQuery(id+"F0.wireOp",EDGE,"E3"),sQuery(id+"F0.wireOp",EDGE,"E4"),sQuery(id+"F0.wireOp",EDGE,"E5"),sQuery(id+"F0.wireOp",EDGE,"E6"),sQuery(id+"F0.wireOp",EDGE,"E7"),sQuery(id+"F0.wireOp",EDGE,"E8"),sQuery(id+"F0.wireOp",EDGE,"E9"),sQuery(id+"F0.wireOp",EDGE,"E10"),sQuery(id+"F0.wireOp",EDGE,"E11"),sQuery(id+"F0.wireOp",EDGE,"E12")])],"isStart":false}),makeQuery(id+"F57.opExtrude","CAP_FACE",FACE,{"disambiguationData":[OSD([sQuery(id+"F56.wireOp",EDGE,"E93"),sQuery(id+"F56.wireOp",EDGE,"E94"),sQuery(id+"F56.wireOp",EDGE,"E95"),sQuery(id+"F56.wireOp",EDGE,"E96")])],"isStart":false})]});
            var sketch = newSketch(context, id + "F58", { "sketchPlane" : qUnion([Q0])});
            skLineSegment(sketch, "E97", {"start": v(-37.24, 15.28) * mm, "end": v(-37.24, 0) * mm});
            skLineSegment(sketch, "E98", {"start": v(-37.24, 0) * mm, "end": v(-64.77, 0) * mm});
            skLineSegment(sketch, "E99", {"start": v(-64.77, 0) * mm, "end": v(-64.77, 15.36) * mm});
            skSolve(sketch);
        }
        {
            var Q0;
            Q0=makeQuery(id+"F58.imprint","IMPRINT",FACE,{"disambiguationData":[TD([[makeQuery(id+"F58.imprint","IMPRINT",EDGE,{"derivedFrom":sQuery(id+"F58.wireOp",EDGE,"E97")}),-1.0]])]});
            extrude(context, id + "F59", {"entities" : qUnion([Q0]), "operationType" : NewBodyOperationType.ADD, "depth" : 0.25 * mm, "offsetDistance" : 25.4 * mm});
        }
        {
            var Q0;
            Q0=makeQuery(id+"F59.opExtrude","CAP_FACE",FACE,{"disambiguationData":[OSD([sQuery(id+"F54.wireOp",EDGE,"E88"),sQuery(id+"F58.wireOp",EDGE,"E97"),sQuery(id+"F58.wireOp",EDGE,"E98"),sQuery(id+"F58.wireOp",EDGE,"E99")])],"isStart":false});
            var sketch = newSketch(context, id + "F60", { "sketchPlane" : qUnion([Q0])});
            skLineSegment(sketch, "E100.bottom", {"start": v(-42.1, 11.64) * mm, "end": v(-38, 11.64) * mm});
            skLineSegment(sketch, "E100.top", {"start": v(-42.1, 10.73) * mm, "end": v(-38, 10.73) * mm});
            skLineSegment(sketch, "E100.left", {"start": v(-42.1, 11.64) * mm, "end": v(-42.1, 10.73) * mm});
            skLineSegment(sketch, "E100.right", {"start": v(-38, 11.64) * mm, "end": v(-38, 10.73) * mm});
            skSolve(sketch);
        }
        {
            var Q0;
            Q0=makeQuery(id+"F60.imprint","IMPRINT",FACE,{"disambiguationData":[TD([[makeQuery(id+"F60.imprint","IMPRINT",EDGE,{"derivedFrom":sQuery(id+"F60.wireOp",EDGE,"E100.bottom")}),-1.0]])]});
            extrude(context, id + "F61", {"entities" : qUnion([Q0]), "operationType" : NewBodyOperationType.ADD, "depth" : 1.27 * mm, "offsetDistance" : 25.4 * mm});
        }
        {
            var Q0;
            Q0=makeQuery(id+"F1.opExtrude","SWEPT_FACE",FACE,{"disambiguationData":[OSD([sQuery(id+"F0.wireOp",EDGE,"E3")])]});
            var sketch = newSketch(context, id + "F62", { "sketchPlane" : qUnion([Q0])});
            skLineSegment(sketch, "E101.bottom", {"start": v(34.74, -33.87) * mm, "end": v(0.72, -33.87) * mm});
            skLineSegment(sketch, "E101.top", {"start": v(34.74, -23.65) * mm, "end": v(0.72, -23.65) * mm});
            skLineSegment(sketch, "E101.left", {"start": v(34.74, -33.87) * mm, "end": v(34.74, -23.65) * mm});
            skLineSegment(sketch, "E101.right", {"start": v(0.72, -33.87) * mm, "end": v(0.72, -23.65) * mm});
            skSolve(sketch);
        }
        {
            var Q0;
            Q0=makeQuery(id+"F62.imprint","IMPRINT",FACE,{"disambiguationData":[TD([[makeQuery(id+"F62.imprint","IMPRINT",EDGE,{"derivedFrom":sQuery(id+"F62.wireOp",EDGE,"E101.bottom")}),-1.0]])]});
            extrude(context, id + "F63", {"entities" : qUnion([Q0]), "operationType" : NewBodyOperationType.REMOVE, "oppositeDirection" : true, "depth" : 0.25 * mm, "offsetDistance" : 25.4 * mm});
        }
        {
            var Q0;
            Q0=makeQuery(id+"F1.opExtrude","CAP_FACE",FACE,{"disambiguationData":[OSD([sQuery(id+"F0.wireOp",EDGE,"E0"),sQuery(id+"F0.wireOp",EDGE,"E2"),sQuery(id+"F0.wireOp",EDGE,"E3"),sQuery(id+"F0.wireOp",EDGE,"E4"),sQuery(id+"F0.wireOp",EDGE,"E5"),sQuery(id+"F0.wireOp",EDGE,"E6"),sQuery(id+"F0.wireOp",EDGE,"E7"),sQuery(id+"F0.wireOp",EDGE,"E8"),sQuery(id+"F0.wireOp",EDGE,"E9"),sQuery(id+"F0.wireOp",EDGE,"E10"),sQuery(id+"F0.wireOp",EDGE,"E11"),sQuery(id+"F0.wireOp",EDGE,"E12")])],"isStart":true});
            var sketch = newSketch(context, id + "F64", { "sketchPlane" : qUnion([Q0])});
            skLineSegment(sketch, "E102", {"start": v(64.4, 15.2) * mm, "end": v(52.62, 21.88) * mm});
            skLineSegment(sketch, "E103", {"start": v(52.62, 21.88) * mm, "end": v(31.87, 21.88) * mm});
            skLineSegment(sketch, "E104", {"start": v(31.87, 21.88) * mm, "end": v(25.75, 15.4) * mm});
            skLineSegment(sketch, "E105", {"start": v(25.75, 15.4) * mm, "end": v(64.4, 15.2) * mm});
            skSolve(sketch);
        }
        {
            var Q0;
            Q0 = qSketchRegion(id + "F64", true);
            extrude(context, id + "F65", {"entities" : qUnion([Q0]), "operationType" : NewBodyOperationType.REMOVE, "oppositeDirection" : true, "depth" : 0.25 * mm, "offsetDistance" : 25.4 * mm});
        }
        {
            var Q0;
            Q0=makeQuery(id+"F65.boolean.opBoolean","COPY",FACE,{"derivedFrom":makeQuery(id+"F65.opExtrude","CAP_FACE",FACE,{"disambiguationData":[OSD([sQuery(id+"F64.wireOp",EDGE,"E102"),sQuery(id+"F64.wireOp",EDGE,"E103"),sQuery(id+"F64.wireOp",EDGE,"E104"),sQuery(id+"F64.wireOp",EDGE,"E105")])],"isStart":false})});
            var sketch = newSketch(context, id + "F66", { "sketchPlane" : qUnion([Q0])});
            skLineSegment(sketch, "E106", {"start": v(37, 21.88) * mm, "end": v(37, 15.34) * mm});
            skLineSegment(sketch, "E107", {"start": v(37, 15.34) * mm, "end": v(38.73, 15.33) * mm});
            skLineSegment(sketch, "E108", {"start": v(38.73, 15.33) * mm, "end": v(38.73, 21.88) * mm});
            skLineSegment(sketch, "E109", {"start": v(38.73, 21.88) * mm, "end": v(37, 21.88) * mm});
            skSolve(sketch);
        }
        {
            var Q0;
            Q0=makeQuery(id+"F66.imprint","IMPRINT",FACE,{"disambiguationData":[TD([[makeQuery(id+"F66.imprint","IMPRINT",EDGE,{"derivedFrom":sQuery(id+"F66.wireOp",EDGE,"E106")}),1.0]])]});
            extrude(context, id + "F67", {"entities" : qUnion([Q0]), "operationType" : NewBodyOperationType.ADD, "depth" : 0.25 * mm, "offsetDistance" : 25.4 * mm});
        }
        {
            var Q0;
            Q0=makeQuery(id+"F67.boolean.opBoolean","MERGE",FACE,{"derivedFrom":[makeQuery(id+"F1.opExtrude","CAP_FACE",FACE,{"disambiguationData":[OSD([sQuery(id+"F0.wireOp",EDGE,"E0"),sQuery(id+"F0.wireOp",EDGE,"E2"),sQuery(id+"F0.wireOp",EDGE,"E3"),sQuery(id+"F0.wireOp",EDGE,"E4"),sQuery(id+"F0.wireOp",EDGE,"E5"),sQuery(id+"F0.wireOp",EDGE,"E6"),sQuery(id+"F0.wireOp",EDGE,"E7"),sQuery(id+"F0.wireOp",EDGE,"E8"),sQuery(id+"F0.wireOp",EDGE,"E9"),sQuery(id+"F0.wireOp",EDGE,"E10"),sQuery(id+"F0.wireOp",EDGE,"E11"),sQuery(id+"F0.wireOp",EDGE,"E12")])],"isStart":true}),makeQuery(id+"F67.opExtrude","CAP_FACE",FACE,{"disambiguationData":[OSD([sQuery(id+"F66.wireOp",EDGE,"E106"),sQuery(id+"F66.wireOp",EDGE,"E107"),sQuery(id+"F66.wireOp",EDGE,"E108"),sQuery(id+"F66.wireOp",EDGE,"E109")])],"isStart":false})]});
            var sketch = newSketch(context, id + "F68", { "sketchPlane" : qUnion([Q0])});
            skLineSegment(sketch, "E110", {"start": v(38.73, 15.33) * mm, "end": v(38.73, 0) * mm});
            skLineSegment(sketch, "E111", {"start": v(38.73, 0) * mm, "end": v(64.68, 0) * mm});
            skLineSegment(sketch, "E112", {"start": v(64.68, 0) * mm, "end": v(64.4, 15.2) * mm});
            skLineSegment(sketch, "E113", {"start": v(64.4, 15.2) * mm, "end": v(38.73, 15.33) * mm});
            skSolve(sketch);
        }
        {
            var Q0;
            Q0 = qSketchRegion(id + "F68", true);
            extrude(context, id + "F69", {"entities" : qUnion([Q0]), "operationType" : NewBodyOperationType.ADD, "depth" : 0.25 * mm, "offsetDistance" : 25.4 * mm});
        }
        {
            var Q0;
            Q0=makeQuery(id+"F69.opExtrude","CAP_FACE",FACE,{"disambiguationData":[OSD([sQuery(id+"F68.wireOp",EDGE,"E110"),sQuery(id+"F68.wireOp",EDGE,"E111"),sQuery(id+"F68.wireOp",EDGE,"E112"),sQuery(id+"F68.wireOp",EDGE,"E113")])],"isStart":false});
            var sketch = newSketch(context, id + "F70", { "sketchPlane" : qUnion([Q0])});
            skLineSegment(sketch, "E114.bottom", {"start": v(39.46, 11.55) * mm, "end": v(42.93, 11.55) * mm});
            skLineSegment(sketch, "E114.top", {"start": v(39.46, 10.73) * mm, "end": v(42.93, 10.73) * mm});
            skLineSegment(sketch, "E114.left", {"start": v(39.46, 11.55) * mm, "end": v(39.46, 10.73) * mm});
            skLineSegment(sketch, "E114.right", {"start": v(42.93, 11.55) * mm, "end": v(42.93, 10.73) * mm});
            skSolve(sketch);
        }
        {
            var Q0;
            Q0 = qSketchRegion(id + "F70", true);
            extrude(context, id + "F71", {"entities" : qUnion([Q0]), "operationType" : NewBodyOperationType.ADD, "depth" : 1.27 * mm, "offsetDistance" : 25.4 * mm});
        }
        {
            var Q0;
            Q0=makeQuery(id+"F1.opExtrude","SWEPT_FACE",FACE,{"disambiguationData":[OSD([sQuery(id+"F0.wireOp",EDGE,"E5")])]});
            var sketch = newSketch(context, id + "F72", { "sketchPlane" : qUnion([Q0])});
            skLineSegment(sketch, "E115.bottom", {"start": v(-35.08, 2.73) * mm, "end": v(-31.7, 2.73) * mm});
            skLineSegment(sketch, "E115.top", {"start": v(-35.08, 3.75) * mm, "end": v(-31.7, 3.75) * mm});
            skLineSegment(sketch, "E115.left", {"start": v(-35.08, 2.73) * mm, "end": v(-35.08, 3.75) * mm});
            skLineSegment(sketch, "E115.right", {"start": v(-31.7, 2.73) * mm, "end": v(-31.7, 3.75) * mm});
            skLineSegment(sketch, "E116.bottom", {"start": v(-0.6, 2.73) * mm, "end": v(-4.06, 2.73) * mm});
            skLineSegment(sketch, "E116.top", {"start": v(-0.6, 3.69) * mm, "end": v(-4.06, 3.69) * mm});
            skLineSegment(sketch, "E116.left", {"start": v(-0.6, 2.73) * mm, "end": v(-0.6, 3.69) * mm});
            skLineSegment(sketch, "E116.right", {"start": v(-4.06, 2.73) * mm, "end": v(-4.06, 3.69) * mm});
            skSolve(sketch);
        }
        {
            var Q0;
            Q0=makeQuery(id+"F72.imprint","IMPRINT",FACE,{"disambiguationData":[TD([[makeQuery(id+"F72.imprint","IMPRINT",EDGE,{"derivedFrom":sQuery(id+"F72.wireOp",EDGE,"E115.bottom")}),1.0]])]});
            var Q1;
            Q1=makeQuery(id+"F72.imprint","IMPRINT",FACE,{"disambiguationData":[TD([[makeQuery(id+"F72.imprint","IMPRINT",EDGE,{"derivedFrom":sQuery(id+"F72.wireOp",EDGE,"E116.bottom")}),1.0]])]});
            extrude(context, id + "F73", {"entities" : qUnion([Q0, Q1]), "operationType" : NewBodyOperationType.REMOVE, "oppositeDirection" : true, "depth" : 12.7 * mm, "offsetDistance" : 25.4 * mm});
        }
        {
            var Q0;
            Q0=makeQuery(id+"F1.opExtrude","SWEPT_FACE",FACE,{"disambiguationData":[OSD([sQuery(id+"F0.wireOp",EDGE,"E5")])]});
            var sketch = newSketch(context, id + "F74", { "sketchPlane" : qUnion([Q0])});
            skLineSegment(sketch, "E117.bottom", {"start": v(-34.7, 14.18) * mm, "end": v(-24.92, 14.18) * mm});
            skLineSegment(sketch, "E117.top", {"start": v(-34.7, 12.22) * mm, "end": v(-24.92, 12.22) * mm});
            skLineSegment(sketch, "E117.left", {"start": v(-34.7, 14.18) * mm, "end": v(-34.7, 12.22) * mm});
            skLineSegment(sketch, "E117.right", {"start": v(-24.92, 14.18) * mm, "end": v(-24.92, 12.22) * mm});
            skLineSegment(sketch, "E118.bottom", {"start": v(-0.74, 14.3) * mm, "end": v(-10.84, 14.3) * mm});
            skLineSegment(sketch, "E118.top", {"start": v(-0.74, 12.22) * mm, "end": v(-10.84, 12.22) * mm});
            skLineSegment(sketch, "E118.left", {"start": v(-0.74, 14.3) * mm, "end": v(-0.74, 12.22) * mm});
            skLineSegment(sketch, "E118.right", {"start": v(-10.84, 14.3) * mm, "end": v(-10.84, 12.22) * mm});
            skSolve(sketch);
        }
        {
            var Q0;
            Q0=makeQuery(id+"F74.imprint","IMPRINT",FACE,{"disambiguationData":[TD([[makeQuery(id+"F74.imprint","IMPRINT",EDGE,{"derivedFrom":sQuery(id+"F74.wireOp",EDGE,"E117.bottom")}),-1.0]])]});
            var Q1;
            Q1=makeQuery(id+"F74.imprint","IMPRINT",FACE,{"disambiguationData":[TD([[makeQuery(id+"F74.imprint","IMPRINT",EDGE,{"derivedFrom":sQuery(id+"F74.wireOp",EDGE,"E118.bottom")}),1.0]])]});
            extrude(context, id + "F75", {"entities" : qUnion([Q0, Q1]), "operationType" : NewBodyOperationType.ADD, "depth" : 0.25 * mm, "offsetDistance" : 25.4 * mm});
        }
        {
            var Q0;
            Q0=makeQuery(id+"F1.opExtrude","SWEPT_FACE",FACE,{"disambiguationData":[OSD([sQuery(id+"F0.wireOp",EDGE,"E11")])]});
            var sketch = newSketch(context, id + "F76", { "sketchPlane" : qUnion([Q0])});
            skLineSegment(sketch, "E119", {"start": v(0, 6.42) * mm, "end": v(35.56, 6.42) * mm, "construction": true});
            skLineSegment(sketch, "E120", {"start": v(35.56, 6.42) * mm, "end": v(31.75, 6.42) * mm, "construction": true});
            skLineSegment(sketch, "E121", {"start": v(31.75, 6.42) * mm, "end": v(26.67, 6.42) * mm, "construction": true});
            skLineSegment(sketch, "E122", {"start": v(0, 6.42) * mm, "end": v(3.81, 6.42) * mm, "construction": true});
            skLineSegment(sketch, "E123", {"start": v(3.81, 6.42) * mm, "end": v(8.9, 6.42) * mm, "construction": true});
            skSolve(sketch);
        }
        {
            var Q0;
            {var subQ0=sQuery(id+"F0.wireOp",EDGE,"E11");Q0=makeQuery(id+"F76.imprint","IMPRINT",FACE,{"disambiguationData":[TD([[makeQuery(id+"F76.imprint","IMPRINT",EDGE,{"derivedFrom":makeQuery(id+"F1.opExtrude","CAP_EDGE",EDGE,{"disambiguationData":[OSD([subQ0])],"isStart":true})}),-1.0]])]});}
            var sketch = newSketch(context, id + "F77", { "sketchPlane" : qUnion([Q0])});
            skCircle(sketch, "E124", {"center": v(3.8, 6.42) * mm, "radius": 2.28 * mm});
            skCircle(sketch, "E125", {"center": v(8.95, 6.42) * mm, "radius": 2.21 * mm});
            skCircle(sketch, "E126", {"center": v(31.83, 6.42) * mm, "radius": 2.33 * mm});
            skCircle(sketch, "E127", {"center": v(26.68, 6.42) * mm, "radius": 2.35 * mm});
            skSolve(sketch);
        }
        {
            var Q0;
            Q0=makeQuery(id+"F77.imprint","IMPRINT",FACE,{"disambiguationData":[TD([[makeQuery(id+"F77.imprint","IMPRINT",EDGE,{"derivedFrom":sQuery(id+"F77.wireOp",EDGE,"E125")}),1.0]])]});
            var Q1;
            Q1=makeQuery(id+"F77.imprint","IMPRINT",FACE,{"disambiguationData":[TD([[makeQuery(id+"F77.imprint","IMPRINT",EDGE,{"derivedFrom":sQuery(id+"F77.wireOp",EDGE,"E127")}),1.0]])]});
            extrude(context, id + "F78", {"entities" : qUnion([Q0, Q1]), "operationType" : NewBodyOperationType.REMOVE, "oppositeDirection" : true, "depth" : 6.35 * mm, "offsetDistance" : 25.4 * mm});
        }
        {
            var Q0;
            {var subQ0=sQuery(id+"F0.wireOp",EDGE,"E11");Q0=makeQuery(id+"F76.imprint","IMPRINT",FACE,{"disambiguationData":[TD([[makeQuery(id+"F76.imprint","IMPRINT",EDGE,{"derivedFrom":makeQuery(id+"F1.opExtrude","CAP_EDGE",EDGE,{"disambiguationData":[OSD([subQ0])],"isStart":true})}),-1.0]])]});}
            var sketch = newSketch(context, id + "F79", { "sketchPlane" : qUnion([Q0])});
            skCircle(sketch, "E128", {"center": v(3.8, 6.42) * mm, "radius": 2.3 * mm});
            skCircle(sketch, "E129", {"center": v(31.83, 6.42) * mm, "radius": 2.21 * mm});
            skSolve(sketch);
        }
        {
            var Q0;
            Q0 = qSketchRegion(id + "F79", true);
            extrude(context, id + "F80", {"entities" : qUnion([Q0]), "operationType" : NewBodyOperationType.ADD, "depth" : 0.25 * mm, "offsetDistance" : 25.4 * mm});
        }
        {
            var Q0;
            {var subQ0=sQuery(id+"F0.wireOp",EDGE,"E11");Q0=makeQuery(id+"F76.imprint","IMPRINT",FACE,{"disambiguationData":[TD([[makeQuery(id+"F76.imprint","IMPRINT",EDGE,{"derivedFrom":makeQuery(id+"F1.opExtrude","CAP_EDGE",EDGE,{"disambiguationData":[OSD([subQ0])],"isStart":true})}),-1.0]])]});}
            var sketch = newSketch(context, id + "F81", { "sketchPlane" : qUnion([Q0])});
            skLineSegment(sketch, "E130.bottom", {"start": v(9.01, 3.1) * mm, "end": v(26.74, 3.1) * mm});
            skLineSegment(sketch, "E130.top", {"start": v(9.01, -1.73) * mm, "end": v(26.74, -1.73) * mm});
            skLineSegment(sketch, "E130.left", {"start": v(9.01, 3.1) * mm, "end": v(9.01, -1.73) * mm});
            skLineSegment(sketch, "E130.right", {"start": v(26.74, 3.1) * mm, "end": v(26.74, -1.73) * mm});
            skSolve(sketch);
        }
        {
            var Q0;
            Q0=makeQuery(id+"F81.imprint","IMPRINT",FACE,{"disambiguationData":[TD([[makeQuery(id+"F81.imprint","IMPRINT",EDGE,{"derivedFrom":sQuery(id+"F81.wireOp",EDGE,"E130.bottom")}),-1.0]])]});
            extrude(context, id + "F82", {"entities" : qUnion([Q0]), "operationType" : NewBodyOperationType.REMOVE, "oppositeDirection" : true, "depth" : 0.25 * mm, "offsetDistance" : 25.4 * mm});
        }
    });
